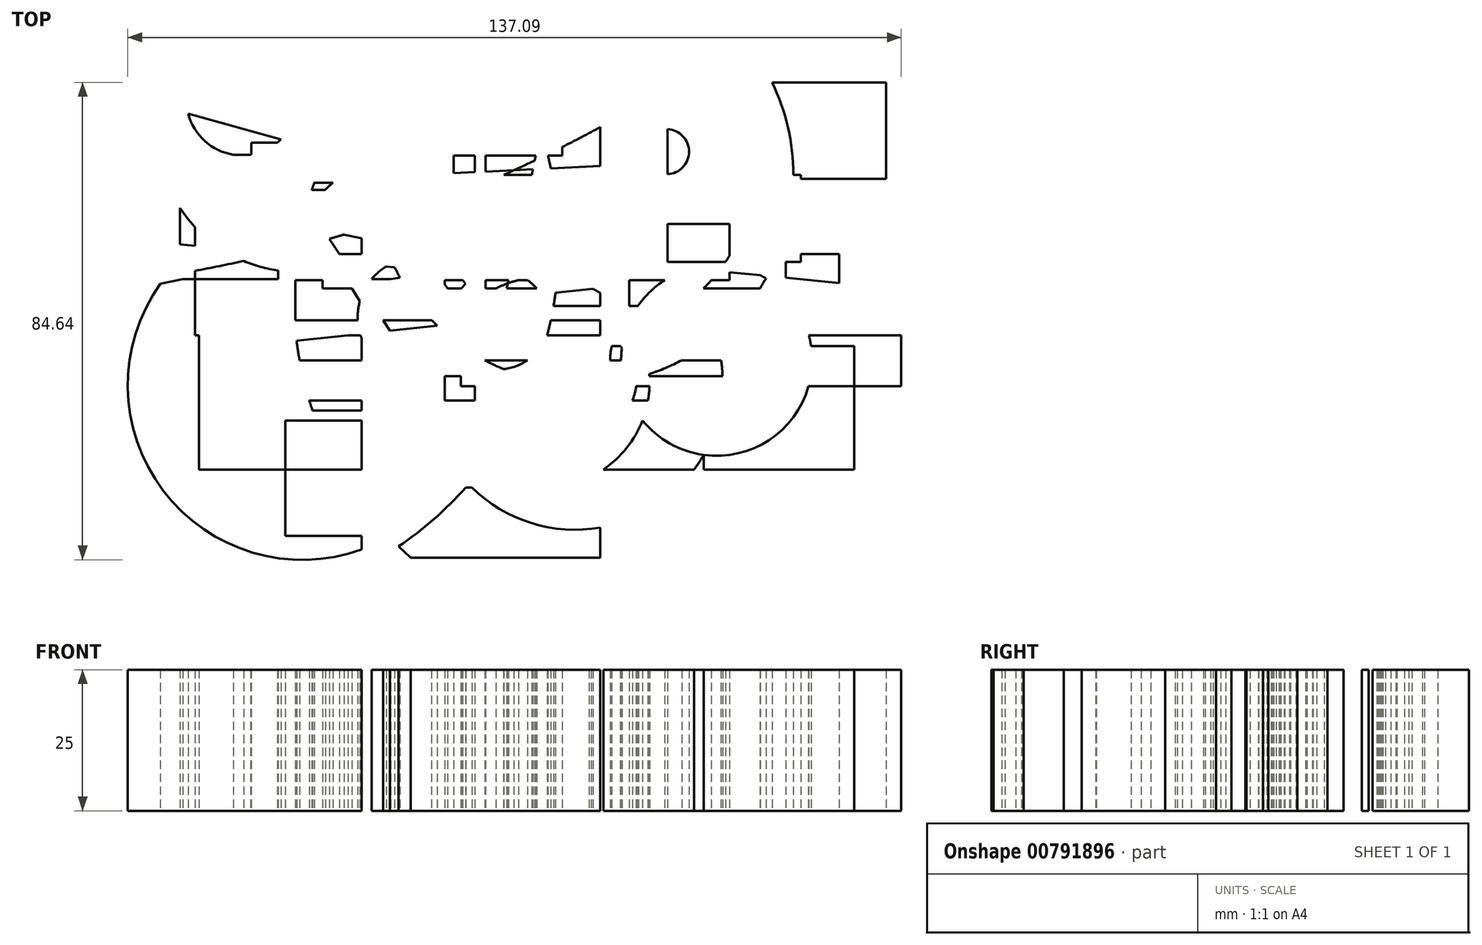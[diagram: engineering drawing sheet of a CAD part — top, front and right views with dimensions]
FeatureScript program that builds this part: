
annotation { "Feature Type Name" : "Feature", "Feature Type Description" : "" }
export const myFeature = defineFeature(function(context is Context, id is Id, definition is map)
    precondition{}
    {
        {
            var Q0;
            Q0=qCreatedBy(makeId("Top.planeOp"),FACE);
            var sketch = newSketch(context, id + "F0", { "sketchPlane" : qUnion([Q0])});
            skLineSegment(sketch, "E0.bottom", {"start": v(-53.43, 52.18) * mm, "end": v(-24.63, 52.18) * mm});
            skLineSegment(sketch, "E0.top", {"start": v(-53.43, 23.56) * mm, "end": v(-24.63, 23.56) * mm});
            skLineSegment(sketch, "E0.left", {"start": v(-53.43, 52.18) * mm, "end": v(-53.43, 23.56) * mm});
            skLineSegment(sketch, "E0.right", {"start": v(-24.63, 52.18) * mm, "end": v(-24.63, 23.56) * mm});
            skLineSegment(sketch, "E1.bottom", {"start": v(13.6, 38.85) * mm, "end": v(-31.38, 38.85) * mm});
            skLineSegment(sketch, "E1.top", {"start": v(13.6, 23.56) * mm, "end": v(-31.38, 23.56) * mm});
            skLineSegment(sketch, "E1.left", {"start": v(13.6, 38.85) * mm, "end": v(13.6, 23.56) * mm});
            skLineSegment(sketch, "E1.right", {"start": v(-31.38, 38.85) * mm, "end": v(-31.38, 23.56) * mm});
            skLineSegment(sketch, "E2.bottom", {"start": v(-41.52, 25.87) * mm, "end": v(-5.6, 25.87) * mm});
            skLineSegment(sketch, "E2.top", {"start": v(-41.52, 4.71) * mm, "end": v(-5.6, 4.71) * mm});
            skLineSegment(sketch, "E2.left", {"start": v(-41.52, 25.87) * mm, "end": v(-41.52, 4.71) * mm});
            skLineSegment(sketch, "E2.right", {"start": v(-5.6, 25.87) * mm, "end": v(-5.6, 4.71) * mm});
            skLineSegment(sketch, "E3.bottom", {"start": v(24.98, 4.71) * mm, "end": v(-33.7, 4.71) * mm});
            skLineSegment(sketch, "E3.top", {"start": v(24.98, -15.56) * mm, "end": v(-33.7, -15.56) * mm});
            skLineSegment(sketch, "E3.left", {"start": v(24.98, 4.71) * mm, "end": v(24.98, -15.56) * mm});
            skLineSegment(sketch, "E3.right", {"start": v(-33.7, 4.71) * mm, "end": v(-33.7, -15.56) * mm});
            skLineSegment(sketch, "E4.bottom", {"start": v(-35.47, -21.6) * mm, "end": v(38.67, -21.6) * mm});
            skLineSegment(sketch, "E4.top", {"start": v(-35.47, -43.83) * mm, "end": v(38.67, -43.83) * mm});
            skLineSegment(sketch, "E4.left", {"start": v(-35.47, -21.6) * mm, "end": v(-35.47, -43.83) * mm});
            skLineSegment(sketch, "E4.right", {"start": v(38.67, -21.6) * mm, "end": v(38.67, -43.83) * mm});
            skLineSegment(sketch, "E5.bottom", {"start": v(85.26, -17.34) * mm, "end": v(-4.36, -17.34) * mm});
            skLineSegment(sketch, "E5.top", {"start": v(85.26, -15.56) * mm, "end": v(-4.36, -15.56) * mm});
            skLineSegment(sketch, "E5.left", {"start": v(85.26, -17.34) * mm, "end": v(85.26, -15.56) * mm});
            skLineSegment(sketch, "E5.right", {"start": v(-4.36, -17.34) * mm, "end": v(-4.36, -15.56) * mm});
            skLineSegment(sketch, "E6.bottom", {"start": v(-50.76, -8.27) * mm, "end": v(95.03, -8.27) * mm});
            skLineSegment(sketch, "E6.top", {"start": v(-50.76, -32.1) * mm, "end": v(95.03, -32.1) * mm});
            skLineSegment(sketch, "E6.left", {"start": v(-50.76, -8.27) * mm, "end": v(-50.76, -32.1) * mm});
            skLineSegment(sketch, "E6.right", {"start": v(95.03, -8.27) * mm, "end": v(95.03, -32.1) * mm});
            skLineSegment(sketch, "E7.bottom", {"start": v(40.1, 55.38) * mm, "end": v(23.74, 55.38) * mm});
            skLineSegment(sketch, "E7.top", {"start": v(40.1, 13.42) * mm, "end": v(23.74, 13.42) * mm});
            skLineSegment(sketch, "E7.left", {"start": v(40.1, 55.38) * mm, "end": v(40.1, 13.42) * mm});
            skLineSegment(sketch, "E7.right", {"start": v(23.74, 55.38) * mm, "end": v(23.74, 13.42) * mm});
            skLineSegment(sketch, "E8.bottom", {"start": v(-13.78, 4.71) * mm, "end": v(55.92, 4.71) * mm});
            skLineSegment(sketch, "E8.top", {"start": v(-13.78, 20.18) * mm, "end": v(55.92, 20.18) * mm});
            skLineSegment(sketch, "E8.left", {"start": v(-13.78, 4.71) * mm, "end": v(-13.78, 20.18) * mm});
            skLineSegment(sketch, "E8.right", {"start": v(55.92, 4.71) * mm, "end": v(55.92, 20.18) * mm});
            skLineSegment(sketch, "E9.bottom", {"start": v(79.39, 19.47) * mm, "end": v(-17.51, 19.47) * mm});
            skLineSegment(sketch, "E9.top", {"start": v(79.39, 11.47) * mm, "end": v(-17.51, 11.47) * mm});
            skLineSegment(sketch, "E9.left", {"start": v(79.39, 19.47) * mm, "end": v(79.39, 11.47) * mm});
            skLineSegment(sketch, "E9.right", {"start": v(-17.51, 19.47) * mm, "end": v(-17.51, 11.47) * mm});
            skLineSegment(sketch, "E10.bottom", {"start": v(-21.96, 34.76) * mm, "end": v(20.36, 34.76) * mm});
            skLineSegment(sketch, "E10.top", {"start": v(-21.96, -47.74) * mm, "end": v(20.36, -47.74) * mm});
            skLineSegment(sketch, "E10.left", {"start": v(-21.96, 34.76) * mm, "end": v(-21.96, -2.78) * mm});
            skLineSegment(sketch, "E10.right", {"start": v(20.36, 34.76) * mm, "end": v(20.36, -47.74) * mm});
            skLineSegment(sketch, "E11.bottom", {"start": v(62.67, 6.13) * mm, "end": v(-28.9, 6.13) * mm});
            skLineSegment(sketch, "E11.top", {"start": v(62.67, 0) * mm, "end": v(-28.9, 0) * mm});
            skLineSegment(sketch, "E11.left", {"start": v(62.67, 6.13) * mm, "end": v(62.67, 0) * mm});
            skLineSegment(sketch, "E11.right", {"start": v(-28.9, 6.13) * mm, "end": v(-28.9, 0) * mm});
            skLineSegment(sketch, "E12.bottom", {"start": v(-40.98, -5.6) * mm, "end": v(73.7, -5.6) * mm});
            skLineSegment(sketch, "E12.top", {"start": v(-40.98, -19.82) * mm, "end": v(73.7, -19.82) * mm});
            skLineSegment(sketch, "E12.left", {"start": v(-40.98, -5.6) * mm, "end": v(-40.98, -19.82) * mm});
            skLineSegment(sketch, "E12.right", {"start": v(73.7, -5.6) * mm, "end": v(73.7, -19.82) * mm});
            skLineSegment(sketch, "E13.bottom", {"start": v(71.03, -3.11) * mm, "end": v(0, -3.11) * mm});
            skLineSegment(sketch, "E13.top", {"start": v(71.03, 36.54) * mm, "end": v(0, 36.54) * mm});
            skLineSegment(sketch, "E13.left", {"start": v(71.03, -3.11) * mm, "end": v(71.03, 36.54) * mm});
            skLineSegment(sketch, "E13.right", {"start": v(0, -3.11) * mm, "end": v(0, 36.54) * mm});
            skLineSegment(sketch, "E14.bottom", {"start": v(-1.87, 32.8) * mm, "end": v(-7.2, 32.8) * mm});
            skLineSegment(sketch, "E14.top", {"start": v(-1.87, -35.3) * mm, "end": v(-7.2, -35.3) * mm});
            skLineSegment(sketch, "E14.left", {"start": v(-1.87, 32.8) * mm, "end": v(-1.87, -35.3) * mm});
            skLineSegment(sketch, "E14.right", {"start": v(-7.2, 32.8) * mm, "end": v(-7.2, -35.3) * mm});
            skLineSegment(sketch, "E15.bottom", {"start": v(-42.58, -23.38) * mm, "end": v(50.94, -23.38) * mm});
            skLineSegment(sketch, "E15.top", {"start": v(-42.58, -12.71) * mm, "end": v(50.94, -12.71) * mm});
            skLineSegment(sketch, "E15.left", {"start": v(-42.58, -23.38) * mm, "end": v(-42.58, -12.71) * mm});
            skLineSegment(sketch, "E15.right", {"start": v(50.94, -23.38) * mm, "end": v(50.94, -12.71) * mm});
            skLineSegment(sketch, "E16.bottom", {"start": v(53.25, -8.27) * mm, "end": v(-51.47, -8.27) * mm});
            skLineSegment(sketch, "E16.top", {"start": v(53.25, 17.16) * mm, "end": v(-51.47, 17.16) * mm});
            skLineSegment(sketch, "E16.left", {"start": v(53.25, -8.27) * mm, "end": v(53.25, 17.16) * mm});
            skLineSegment(sketch, "E16.right", {"start": v(-51.47, -8.27) * mm, "end": v(-51.47, 17.16) * mm});
            skLineSegment(sketch, "E17.bottom", {"start": v(-36.72, 17.51) * mm, "end": v(43.3, 17.51) * mm});
            skLineSegment(sketch, "E17.top", {"start": v(-36.72, 1.51) * mm, "end": v(43.3, 1.51) * mm});
            skLineSegment(sketch, "E17.left", {"start": v(-36.72, 17.51) * mm, "end": v(-36.72, 1.51) * mm});
            skLineSegment(sketch, "E17.right", {"start": v(43.3, 17.51) * mm, "end": v(43.3, 1.51) * mm});
            skLineSegment(sketch, "E18.bottom", {"start": v(65.34, -10.22) * mm, "end": v(-15.56, -10.22) * mm});
            skLineSegment(sketch, "E18.top", {"start": v(65.34, -32.1) * mm, "end": v(-15.56, -32.1) * mm});
            skLineSegment(sketch, "E18.left", {"start": v(65.34, -10.22) * mm, "end": v(65.34, -32.1) * mm});
            skLineSegment(sketch, "E18.right", {"start": v(-15.56, -10.22) * mm, "end": v(-15.56, -32.1) * mm});
            skLineSegment(sketch, "E19.bottom", {"start": v(-54.14, 1.69) * mm, "end": v(25.51, 1.69) * mm});
            skLineSegment(sketch, "E19.top", {"start": v(-54.14, 67.48) * mm, "end": v(25.51, 67.48) * mm});
            skLineSegment(sketch, "E19.left", {"start": v(-54.14, 1.69) * mm, "end": v(-54.14, 67.48) * mm});
            skLineSegment(sketch, "E19.right", {"start": v(25.51, 1.69) * mm, "end": v(25.51, 67.48) * mm});
            skLineSegment(sketch, "E20.bottom", {"start": v(25.51, 45.25) * mm, "end": v(32.27, 45.25) * mm});
            skLineSegment(sketch, "E20.top", {"start": v(25.51, -3.11) * mm, "end": v(32.27, -3.11) * mm});
            skLineSegment(sketch, "E20.left", {"start": v(25.51, 45.25) * mm, "end": v(25.51, -3.11) * mm});
            skLineSegment(sketch, "E20.right", {"start": v(32.27, 45.25) * mm, "end": v(32.27, -3.11) * mm});
            skLineSegment(sketch, "E21.bottom", {"start": v(-12, 23.74) * mm, "end": v(-55.56, 23.74) * mm});
            skLineSegment(sketch, "E21.top", {"start": v(-12, 18.76) * mm, "end": v(-55.56, 18.76) * mm});
            skLineSegment(sketch, "E21.left", {"start": v(-12, 23.74) * mm, "end": v(-12, 18.76) * mm});
            skLineSegment(sketch, "E21.right", {"start": v(-55.56, 23.74) * mm, "end": v(-55.56, 18.76) * mm});
            skCircle(sketch, "E22", {"center": v(-33.16, 28) * mm, "radius": 25.06 * mm});
            skCircle(sketch, "E23", {"center": v(14.31, 24.1) * mm, "radius": 34.24 * mm});
            skCircle(sketch, "E24", {"center": v(-51.83, 7.91) * mm, "radius": 64.83 * mm});
            skCircle(sketch, "E25", {"center": v(27.3, -1.87) * mm, "radius": 61.2 * mm});
            skArc(sketch, "E26", {"start": v(-2.22, -8.27) * mm, "mid": v(-21.98, -1.4) * mm, "end": v(-2.56, -9.18) * mm});
            skCircle(sketch, "E27", {"center": v(2.4, -5.6) * mm, "radius": 8.71 * mm});
            skCircle(sketch, "E28", {"center": v(40.98, -12.71) * mm, "radius": 16.93 * mm});
            skCircle(sketch, "E29", {"center": v(10.4, -16.62) * mm, "radius": 18.7 * mm});
            skCircle(sketch, "E30", {"center": v(34.4, -12.9) * mm, "radius": 12.31 * mm});
            skCircle(sketch, "E31", {"center": v(18.58, -16.45) * mm, "radius": 8.18 * mm});
            skCircle(sketch, "E32", {"center": v(10.93, -16.62) * mm, "radius": 4.98 * mm});
            skCircle(sketch, "E33", {"center": v(15.91, -16.62) * mm, "radius": 26.15 * mm});
            skArc(sketch, "E34", {"start": v(-13.78, 7.51) * mm, "mid": v(-57.86, -34.81) * mm, "end": v(-2.81, -8.27) * mm});
            skCircle(sketch, "E35", {"center": v(32.1, 24.27) * mm, "radius": 4 * mm});
            skCircle(sketch, "E36", {"center": v(17.34, 20.18) * mm, "radius": 37.24 * mm});
            skCircle(sketch, "E37", {"center": v(-22.5, 12.53) * mm, "radius": 7.7 * mm});
            skArc(sketch, "E38", {"start": v(-48.45, 41.7) * mm, "mid": v(-47.9, 24.84) * mm, "end": v(-33.34, 33.34) * mm});
            skArc(sketch, "E39", {"start": v(-2.04, 17.87) * mm, "mid": v(21.17, 29.08) * mm, "end": v(43.05, 42.7) * mm});
            skLineSegment(sketch, "E40", {"start": v(-33.52, 45.6) * mm, "end": v(-9.16, 14.5) * mm});
            skLineSegment(sketch, "E41", {"start": v(35.47, 22.5) * mm, "end": v(-32.27, 19.11) * mm});
            skLineSegment(sketch, "E42", {"start": v(-53.96, 31.38) * mm, "end": v(-10.58, 19.3) * mm});
            skLineSegment(sketch, "E43", {"start": v(20.71, 30.31) * mm, "end": v(-39.92, 19.82) * mm});
            skLineSegment(sketch, "E44", {"start": v(-37.43, 23.56) * mm, "end": v(-14.5, -11.11) * mm});
            skLineSegment(sketch, "E45", {"start": v(16.62, 21.42) * mm, "end": v(-29.07, 8.98) * mm});
            skLineSegment(sketch, "E46", {"start": v(-45.25, 13.96) * mm, "end": v(-21.96, 8.9) * mm});
            skLineSegment(sketch, "E47", {"start": v(34.94, 1.51) * mm, "end": v(-15.38, -3.47) * mm});
            skLineSegment(sketch, "E48", {"start": v(-45.78, -10.58) * mm, "end": v(-4.53, -6.13) * mm});
            skLineSegment(sketch, "E49", {"start": v(25.16, 8.09) * mm, "end": v(-19.11, 1.33) * mm});
            skLineSegment(sketch, "E50", {"start": v(-52.54, 5.96) * mm, "end": v(5.25, 15.74) * mm});
            skLineSegment(sketch, "E51", {"start": v(-42.23, 4.18) * mm, "end": v(-104.28, -9.33) * mm});
            skLineSegment(sketch, "E52", {"start": v(-62.85, 8.8) * mm, "end": v(-28.9, 5.14) * mm});
            skLineSegment(sketch, "E53", {"start": v(62.85, 0.98) * mm, "end": v(-14.31, 8.45) * mm});
            skLineSegment(sketch, "E54", {"start": v(-38.5, 23.74) * mm, "end": v(4.53, -45.25) * mm});
            skLineSegment(sketch, "E55", {"start": v(10.4, 30.31) * mm, "end": v(2.76, -4.71) * mm});
            skLineSegment(sketch, "E56", {"start": v(-0.98, 21.07) * mm, "end": v(-8.09, 15.56) * mm});
            skLineSegment(sketch, "E57.trimOffspring", {"start": v(-26.75, 4.9) * mm, "end": v(4.71, 1.51) * mm});
            skArc(sketch, "E58.trimOffspring", {"start": v(-3.75, -5.6) * mm, "mid": v(-7.6, 1.28) * mm, "end": v(-13.07, 6.96) * mm});
            skArc(sketch, "E59.trimOffspring", {"start": v(-51.47, 3.14) * mm, "mid": v(-35.15, 6.75) * mm, "end": v(-19.11, 11.47) * mm});
            skLineSegment(sketch, "E60.trimOffspring", {"start": v(-21.96, -5.6) * mm, "end": v(-21.96, -47.74) * mm});
            skLineSegment(sketch, "E61.trimOffspring", {"start": v(-18.02, 8.04) * mm, "end": v(3.82, 3.29) * mm});
            skSolve(sketch);
        }
        {
            var Q0;
            {var subQ6=sQuery(id+"F0.wireOp",EDGE,"E2.left");var subQ7=sQuery(id+"F0.wireOp",EDGE,"E2.bottom");var subQ8=makeQuery(id+"F0.imprint","INTERSECT",VERTEX,{"derivedFrom":[subQ7,subQ6]});Q0=makeQuery(id+"F0.imprint","IMPRINT",FACE,{"disambiguationData":[TD([[makeQuery(id+"F0.imprint","IMPRINT",EDGE,{"disambiguationData":[TD([[subQ8,-1.0]])],"derivedFrom":subQ7}),1.0]])]});}
            var Q1;
            {var subQ0=sQuery(id+"F0.wireOp",EDGE,"E25");var subQ1=sQuery(id+"F0.wireOp",EDGE,"E17.bottom");var subQ2=makeQuery(id+"F0.imprint","INTERSECT",VERTEX,{"derivedFrom":[subQ1,subQ0]});Q1=makeQuery(id+"F0.imprint","IMPRINT",FACE,{"disambiguationData":[TD([[makeQuery(id+"F0.imprint","IMPRINT",EDGE,{"disambiguationData":[TD([[subQ2,-1.0]])],"derivedFrom":subQ1}),1.0]])]});}
            var Q2;
            {var subQ1=sQuery(id+"F0.wireOp",EDGE,"E19.bottom");var subQ5=sQuery(id+"F0.wireOp",EDGE,"E26");var subQ6=makeQuery(id+"F0.imprint","INTERSECT",VERTEX,{"disambiguationData":[OD(0.0)],"derivedFrom":[subQ1,subQ5]});Q2=makeQuery(id+"F0.imprint","IMPRINT",FACE,{"disambiguationData":[TD([[makeQuery(id+"F0.imprint","IMPRINT",EDGE,{"disambiguationData":[TD([[subQ6,-1.0]])],"derivedFrom":subQ1}),1.0]])]});}
            var Q3;
            {var subQ5=sQuery(id+"F0.wireOp",EDGE,"E27");var subQ6=sQuery(id+"F0.wireOp",EDGE,"E11.top");var subQ7=makeQuery(id+"F0.imprint","INTERSECT",VERTEX,{"disambiguationData":[OD(1.0)],"derivedFrom":[subQ6,subQ5]});Q3=makeQuery(id+"F0.imprint","IMPRINT",FACE,{"disambiguationData":[TD([[makeQuery(id+"F0.imprint","IMPRINT",EDGE,{"disambiguationData":[TD([[subQ7,-1.0]])],"derivedFrom":subQ6}),-1.0]])]});}
            var Q4;
            {var subQ0=sQuery(id+"F0.wireOp",EDGE,"E29");var subQ1=sQuery(id+"F0.wireOp",EDGE,"E11.top");var subQ2=makeQuery(id+"F0.imprint","INTERSECT",VERTEX,{"disambiguationData":[OD(1.0)],"derivedFrom":[subQ1,subQ0]});Q4=makeQuery(id+"F0.imprint","IMPRINT",FACE,{"disambiguationData":[TD([[makeQuery(id+"F0.imprint","IMPRINT",EDGE,{"disambiguationData":[TD([[subQ2,-1.0]])],"derivedFrom":subQ1}),-1.0]])]});}
            var Q5;
            {var subQ0=sQuery(id+"F0.wireOp",EDGE,"E27");var subQ1=sQuery(id+"F0.wireOp",EDGE,"E11.top");var subQ2=makeQuery(id+"F0.imprint","INTERSECT",VERTEX,{"disambiguationData":[OD(0.0)],"derivedFrom":[subQ1,subQ0]});Q5=makeQuery(id+"F0.imprint","IMPRINT",FACE,{"disambiguationData":[TD([[makeQuery(id+"F0.imprint","IMPRINT",EDGE,{"disambiguationData":[TD([[subQ2,-1.0]])],"derivedFrom":subQ1}),-1.0]])]});}
            var Q6;
            {var subQ0=sQuery(id+"F0.wireOp",EDGE,"E31");var subQ1=sQuery(id+"F0.wireOp",EDGE,"E18.bottom");var subQ2=makeQuery(id+"F0.imprint","INTERSECT",VERTEX,{"disambiguationData":[OD(1.0)],"derivedFrom":[subQ1,subQ0]});Q6=makeQuery(id+"F0.imprint","IMPRINT",FACE,{"disambiguationData":[TD([[makeQuery(id+"F0.imprint","IMPRINT",EDGE,{"disambiguationData":[TD([[subQ2,-1.0]])],"derivedFrom":subQ1}),1.0]])]});}
            var Q7;
            {var subQ0=sQuery(id+"F0.wireOp",EDGE,"E36");var subQ1=sQuery(id+"F0.wireOp",EDGE,"E15.top");var subQ2=makeQuery(id+"F0.imprint","INTERSECT",VERTEX,{"disambiguationData":[OD(0.0)],"derivedFrom":[subQ1,subQ0]});Q7=makeQuery(id+"F0.imprint","IMPRINT",FACE,{"disambiguationData":[TD([[makeQuery(id+"F0.imprint","IMPRINT",EDGE,{"disambiguationData":[TD([[subQ2,-1.0]])],"derivedFrom":subQ1}),-1.0]])]});}
            var Q8;
            {var subQ0=sQuery(id+"F0.wireOp",EDGE,"E44");var subQ1=sQuery(id+"F0.wireOp",EDGE,"E12.bottom");var subQ2=makeQuery(id+"F0.imprint","INTERSECT",VERTEX,{"derivedFrom":[subQ1,subQ0]});Q8=makeQuery(id+"F0.imprint","IMPRINT",FACE,{"disambiguationData":[TD([[makeQuery(id+"F0.imprint","IMPRINT",EDGE,{"disambiguationData":[TD([[subQ2,-1.0]])],"derivedFrom":subQ1}),-1.0]])]});}
            var Q9;
            {var subQ0=sQuery(id+"F0.wireOp",EDGE,"E25");var subQ1=sQuery(id+"F0.wireOp",EDGE,"E6.top");var subQ2=makeQuery(id+"F0.imprint","INTERSECT",VERTEX,{"disambiguationData":[OD(1.0)],"derivedFrom":[subQ1,subQ0]});Q9=makeQuery(id+"F0.imprint","IMPRINT",FACE,{"disambiguationData":[TD([[makeQuery(id+"F0.imprint","IMPRINT",EDGE,{"disambiguationData":[TD([[subQ2,-1.0]])],"derivedFrom":subQ1}),1.0]])]});}
            var Q10;
            {var subQ0=sQuery(id+"F0.wireOp",EDGE,"E15.bottom");var subQ1=sQuery(id+"F0.wireOp",EDGE,"E4.left");var subQ2=makeQuery(id+"F0.imprint","INTERSECT",VERTEX,{"derivedFrom":[subQ1,subQ0]});Q10=makeQuery(id+"F0.imprint","IMPRINT",FACE,{"disambiguationData":[TD([[makeQuery(id+"F0.imprint","IMPRINT",EDGE,{"disambiguationData":[TD([[subQ2,-1.0]])],"derivedFrom":subQ1}),1.0]])]});}
            var Q11;
            {var subQ0=sQuery(id+"F0.wireOp",EDGE,"E29");var subQ9=sQuery(id+"F0.wireOp",EDGE,"E10.right");var subQ10=makeQuery(id+"F0.imprint","INTERSECT",VERTEX,{"disambiguationData":[OD(1.0)],"derivedFrom":[subQ9,subQ0]});Q11=makeQuery(id+"F0.imprint","IMPRINT",FACE,{"disambiguationData":[TD([[makeQuery(id+"F0.imprint","IMPRINT",EDGE,{"disambiguationData":[TD([[subQ10,-1.0]])],"derivedFrom":subQ9}),-1.0]])]});}
            var Q12;
            {var subQ3=sQuery(id+"F0.wireOp",EDGE,"E54");var subQ6=sQuery(id+"F0.wireOp",EDGE,"E4.top");var subQ9=makeQuery(id+"F0.imprint","INTERSECT",VERTEX,{"derivedFrom":[subQ6,subQ3]});Q12=makeQuery(id+"F0.imprint","IMPRINT",FACE,{"disambiguationData":[TD([[makeQuery(id+"F0.imprint","IMPRINT",EDGE,{"disambiguationData":[TD([[subQ9,1.0]])],"derivedFrom":subQ6}),1.0]])]});}
            var Q13;
            {var subQ3=sQuery(id+"F0.wireOp",EDGE,"E4.top");var subQ7=makeQuery(id+"F0.imprint","INTERSECT",VERTEX,{"derivedFrom":[subQ3,sQuery(id+"F0.wireOp",EDGE,"E54")]});Q13=makeQuery(id+"F0.imprint","IMPRINT",FACE,{"disambiguationData":[TD([[makeQuery(id+"F0.imprint","IMPRINT",EDGE,{"disambiguationData":[TD([[subQ7,1.0]])],"derivedFrom":subQ3}),-1.0]])]});}
            var Q14;
            {var subQ0=sQuery(id+"F0.wireOp",EDGE,"E28");var subQ1=sQuery(id+"F0.wireOp",EDGE,"E4.right");var subQ2=makeQuery(id+"F0.imprint","INTERSECT",VERTEX,{"derivedFrom":[subQ1,subQ0]});Q14=makeQuery(id+"F0.imprint","IMPRINT",FACE,{"disambiguationData":[TD([[makeQuery(id+"F0.imprint","IMPRINT",EDGE,{"disambiguationData":[TD([[subQ2,-1.0]])],"derivedFrom":subQ1}),-1.0]])]});}
            var Q15;
            {var subQ0=sQuery(id+"F0.wireOp",EDGE,"E29");var subQ1=sQuery(id+"F0.wireOp",EDGE,"E5.bottom");var subQ2=makeQuery(id+"F0.imprint","INTERSECT",VERTEX,{"derivedFrom":[subQ1,subQ0]});Q15=makeQuery(id+"F0.imprint","IMPRINT",FACE,{"disambiguationData":[TD([[makeQuery(id+"F0.imprint","IMPRINT",EDGE,{"disambiguationData":[TD([[subQ2,-1.0]])],"derivedFrom":subQ1}),1.0]])]});}
            var Q16;
            {var subQ1=sQuery(id+"F0.wireOp",EDGE,"E16.bottom");var subQ7=sQuery(id+"F0.wireOp",EDGE,"E33");var subQ8=makeQuery(id+"F0.imprint","INTERSECT",VERTEX,{"disambiguationData":[OD(0.0)],"derivedFrom":[subQ1,subQ7]});Q16=makeQuery(id+"F0.imprint","IMPRINT",FACE,{"disambiguationData":[TD([[makeQuery(id+"F0.imprint","IMPRINT",EDGE,{"disambiguationData":[TD([[subQ8,-1.0]])],"derivedFrom":subQ1}),1.0]])]});}
            var Q17;
            {var subQ1=sQuery(id+"F0.wireOp",EDGE,"E11.top");var subQ9=sQuery(id+"F0.wireOp",EDGE,"E36");var subQ10=makeQuery(id+"F0.imprint","INTERSECT",VERTEX,{"disambiguationData":[OD(0.0)],"derivedFrom":[subQ1,subQ9]});Q17=makeQuery(id+"F0.imprint","IMPRINT",FACE,{"disambiguationData":[TD([[makeQuery(id+"F0.imprint","IMPRINT",EDGE,{"disambiguationData":[TD([[subQ10,-1.0]])],"derivedFrom":subQ1}),-1.0]])]});}
            var Q18;
            {var subQ5=sQuery(id+"F0.wireOp",EDGE,"E20.right");var subQ7=sQuery(id+"F0.wireOp",EDGE,"E8.bottom");var subQ8=makeQuery(id+"F0.imprint","INTERSECT",VERTEX,{"derivedFrom":[subQ7,subQ5]});Q18=makeQuery(id+"F0.imprint","IMPRINT",FACE,{"disambiguationData":[TD([[makeQuery(id+"F0.imprint","IMPRINT",EDGE,{"disambiguationData":[TD([[subQ8,-1.0]])],"derivedFrom":subQ7}),1.0]])]});}
            var Q19;
            {var subQ0=sQuery(id+"F0.wireOp",EDGE,"E33");var subQ1=sQuery(id+"F0.wireOp",EDGE,"E10.right");var subQ2=makeQuery(id+"F0.imprint","INTERSECT",VERTEX,{"disambiguationData":[OD(0.0)],"derivedFrom":[subQ1,subQ0]});Q19=makeQuery(id+"F0.imprint","IMPRINT",FACE,{"disambiguationData":[TD([[makeQuery(id+"F0.imprint","IMPRINT",EDGE,{"disambiguationData":[TD([[subQ2,-1.0]])],"derivedFrom":subQ1}),-1.0]])]});}
            var Q20;
            {var subQ1=sQuery(id+"F0.wireOp",EDGE,"E10.right");var subQ5=sQuery(id+"F0.wireOp",EDGE,"E12.bottom");var subQ6=makeQuery(id+"F0.imprint","INTERSECT",VERTEX,{"derivedFrom":[subQ1,subQ5]});Q20=makeQuery(id+"F0.imprint","IMPRINT",FACE,{"disambiguationData":[TD([[makeQuery(id+"F0.imprint","IMPRINT",EDGE,{"disambiguationData":[TD([[subQ6,-1.0]])],"derivedFrom":subQ1}),-1.0]])]});}
            var Q21;
            {var subQ0=sQuery(id+"F0.wireOp",EDGE,"E18.left");var subQ1=sQuery(id+"F0.wireOp",EDGE,"E5.bottom");var subQ2=makeQuery(id+"F0.imprint","INTERSECT",VERTEX,{"derivedFrom":[subQ1,subQ0]});Q21=makeQuery(id+"F0.imprint","IMPRINT",FACE,{"disambiguationData":[TD([[makeQuery(id+"F0.imprint","IMPRINT",EDGE,{"disambiguationData":[TD([[subQ2,-1.0]])],"derivedFrom":subQ1}),1.0]])]});}
            var Q22;
            {var subQ0=sQuery(id+"F0.wireOp",EDGE,"E12.right");var subQ1=sQuery(id+"F0.wireOp",EDGE,"E5.bottom");var subQ2=makeQuery(id+"F0.imprint","INTERSECT",VERTEX,{"derivedFrom":[subQ1,subQ0]});Q22=makeQuery(id+"F0.imprint","IMPRINT",FACE,{"disambiguationData":[TD([[makeQuery(id+"F0.imprint","IMPRINT",EDGE,{"disambiguationData":[TD([[subQ2,-1.0]])],"derivedFrom":subQ1}),-1.0]])]});}
            var Q23;
            {var subQ5=sQuery(id+"F0.wireOp",EDGE,"E12.right");var subQ6=sQuery(id+"F0.wireOp",EDGE,"E5.top");var subQ7=makeQuery(id+"F0.imprint","INTERSECT",VERTEX,{"derivedFrom":[subQ6,subQ5]});Q23=makeQuery(id+"F0.imprint","IMPRINT",FACE,{"disambiguationData":[TD([[makeQuery(id+"F0.imprint","IMPRINT",EDGE,{"disambiguationData":[TD([[subQ7,-1.0]])],"derivedFrom":subQ6}),-1.0]])]});}
            var Q24;
            {var subQ7=sQuery(id+"F0.wireOp",EDGE,"E4.right");var subQ9=sQuery(id+"F0.wireOp",EDGE,"E33");var subQ10=makeQuery(id+"F0.imprint","INTERSECT",VERTEX,{"derivedFrom":[subQ7,subQ9]});Q24=makeQuery(id+"F0.imprint","IMPRINT",FACE,{"disambiguationData":[TD([[makeQuery(id+"F0.imprint","IMPRINT",EDGE,{"disambiguationData":[TD([[subQ10,-1.0]])],"derivedFrom":subQ7}),1.0]])]});}
            var Q25;
            {var subQ1=sQuery(id+"F0.wireOp",EDGE,"E5.top");var subQ7=sQuery(id+"F0.wireOp",EDGE,"E33");var subQ9=makeQuery(id+"F0.imprint","INTERSECT",VERTEX,{"derivedFrom":[subQ1,subQ7]});Q25=makeQuery(id+"F0.imprint","IMPRINT",FACE,{"disambiguationData":[TD([[makeQuery(id+"F0.imprint","IMPRINT",EDGE,{"disambiguationData":[TD([[subQ9,-1.0]])],"derivedFrom":subQ1}),-1.0]])]});}
            var Q26;
            {var subQ5=sQuery(id+"F0.wireOp",EDGE,"E5.right");Q26=makeQuery(id+"F0.imprint","IMPRINT",FACE,{"disambiguationData":[TD([[makeQuery(id+"F0.imprint","IMPRINT",EDGE,{"derivedFrom":subQ5}),1.0]])]});}
            var Q27;
            {var subQ0=sQuery(id+"F0.wireOp",EDGE,"E25");var subQ1=sQuery(id+"F0.wireOp",EDGE,"E4.bottom");var subQ2=makeQuery(id+"F0.imprint","INTERSECT",VERTEX,{"derivedFrom":[subQ1,subQ0]});Q27=makeQuery(id+"F0.imprint","IMPRINT",FACE,{"disambiguationData":[TD([[makeQuery(id+"F0.imprint","IMPRINT",EDGE,{"disambiguationData":[TD([[subQ2,-1.0]])],"derivedFrom":subQ1}),1.0]])]});}
            var Q28;
            {var subQ5=sQuery(id+"F0.wireOp",EDGE,"E46");var subQ6=sQuery(id+"F0.wireOp",EDGE,"E10.left");var subQ7=makeQuery(id+"F0.imprint","INTERSECT",VERTEX,{"derivedFrom":[subQ6,subQ5]});Q28=makeQuery(id+"F0.imprint","IMPRINT",FACE,{"disambiguationData":[TD([[makeQuery(id+"F0.imprint","IMPRINT",EDGE,{"disambiguationData":[TD([[subQ7,-1.0]])],"derivedFrom":subQ6}),-1.0]])]});}
            var Q29;
            {var subQ5=sQuery(id+"F0.wireOp",EDGE,"E55");var subQ6=sQuery(id+"F0.wireOp",EDGE,"E1.top");var subQ7=makeQuery(id+"F0.imprint","INTERSECT",VERTEX,{"derivedFrom":[subQ6,subQ5]});Q29=makeQuery(id+"F0.imprint","IMPRINT",FACE,{"disambiguationData":[TD([[makeQuery(id+"F0.imprint","IMPRINT",EDGE,{"disambiguationData":[TD([[subQ7,-1.0]])],"derivedFrom":subQ6}),1.0]])]});}
            var Q30;
            {var subQ6=sQuery(id+"F0.wireOp",EDGE,"E1.top");var subQ9=sQuery(id+"F0.wireOp",EDGE,"E1.left");var subQ10=makeQuery(id+"F0.imprint","INTERSECT",VERTEX,{"derivedFrom":[subQ6,subQ9]});Q30=makeQuery(id+"F0.imprint","IMPRINT",FACE,{"disambiguationData":[TD([[makeQuery(id+"F0.imprint","IMPRINT",EDGE,{"disambiguationData":[TD([[subQ10,-1.0]])],"derivedFrom":subQ6}),1.0]])]});}
            var Q31;
            {var subQ0=sQuery(id+"F0.wireOp",EDGE,"E39");var subQ1=sQuery(id+"F0.wireOp",EDGE,"E20.left");var subQ2=makeQuery(id+"F0.imprint","INTERSECT",VERTEX,{"derivedFrom":[subQ1,subQ0]});Q31=makeQuery(id+"F0.imprint","IMPRINT",FACE,{"disambiguationData":[TD([[makeQuery(id+"F0.imprint","IMPRINT",EDGE,{"disambiguationData":[TD([[subQ2,-1.0]])],"derivedFrom":subQ1}),1.0]])]});}
            var Q32;
            {var subQ0=sQuery(id+"F0.wireOp",EDGE,"E17.right");var subQ1=sQuery(id+"F0.wireOp",EDGE,"E9.top");var subQ2=makeQuery(id+"F0.imprint","INTERSECT",VERTEX,{"derivedFrom":[subQ1,subQ0]});Q32=makeQuery(id+"F0.imprint","IMPRINT",FACE,{"disambiguationData":[TD([[makeQuery(id+"F0.imprint","IMPRINT",EDGE,{"disambiguationData":[TD([[subQ2,-1.0]])],"derivedFrom":subQ1}),1.0]])]});}
            var Q33;
            {var subQ0=sQuery(id+"F0.wireOp",EDGE,"E28");var subQ1=sQuery(id+"F0.wireOp",EDGE,"E11.top");var subQ2=makeQuery(id+"F0.imprint","INTERSECT",VERTEX,{"disambiguationData":[OD(0.0)],"derivedFrom":[subQ1,subQ0]});Q33=makeQuery(id+"F0.imprint","IMPRINT",FACE,{"disambiguationData":[TD([[makeQuery(id+"F0.imprint","IMPRINT",EDGE,{"disambiguationData":[TD([[subQ2,-1.0]])],"derivedFrom":subQ1}),1.0]])]});}
            var Q34;
            {var subQ5=sQuery(id+"F0.wireOp",EDGE,"E8.right");var subQ7=sQuery(id+"F0.wireOp",EDGE,"E8.bottom");var subQ8=makeQuery(id+"F0.imprint","INTERSECT",VERTEX,{"derivedFrom":[subQ7,subQ5]});Q34=makeQuery(id+"F0.imprint","IMPRINT",FACE,{"disambiguationData":[TD([[makeQuery(id+"F0.imprint","IMPRINT",EDGE,{"disambiguationData":[TD([[subQ8,1.0]])],"derivedFrom":subQ7}),-1.0]])]});}
            var Q35;
            {var subQ1=sQuery(id+"F0.wireOp",EDGE,"E8.right");var subQ5=sQuery(id+"F0.wireOp",EDGE,"E8.top");var subQ6=makeQuery(id+"F0.imprint","INTERSECT",VERTEX,{"derivedFrom":[subQ5,subQ1]});Q35=makeQuery(id+"F0.imprint","IMPRINT",FACE,{"disambiguationData":[TD([[makeQuery(id+"F0.imprint","IMPRINT",EDGE,{"disambiguationData":[TD([[subQ6,1.0]])],"derivedFrom":subQ5}),1.0]])]});}
            var Q36;
            {var subQ0=sQuery(id+"F0.wireOp",EDGE,"E20.right");var subQ1=makeQuery(id+"F0.imprint","INTERSECT",VERTEX,{"derivedFrom":[subQ0,sQuery(id+"F0.wireOp",EDGE,"E41")]});Q36=makeQuery(id+"F0.imprint","IMPRINT",FACE,{"disambiguationData":[TD([[makeQuery(id+"F0.imprint","IMPRINT",EDGE,{"disambiguationData":[TD([[subQ1,1.0]])],"derivedFrom":subQ0}),1.0]])]});}
            var Q37;
            {var subQ0=sQuery(id+"F0.wireOp",EDGE,"E39");var subQ1=sQuery(id+"F0.wireOp",EDGE,"E8.top");var subQ2=makeQuery(id+"F0.imprint","INTERSECT",VERTEX,{"derivedFrom":[subQ1,subQ0]});Q37=makeQuery(id+"F0.imprint","IMPRINT",FACE,{"disambiguationData":[TD([[makeQuery(id+"F0.imprint","IMPRINT",EDGE,{"disambiguationData":[TD([[subQ2,-1.0]])],"derivedFrom":subQ1}),1.0]])]});}
            var Q38;
            {var subQ0=sQuery(id+"F0.wireOp",EDGE,"E14.left");var subQ1=sQuery(id+"F0.wireOp",EDGE,"E1.top");var subQ2=makeQuery(id+"F0.imprint","INTERSECT",VERTEX,{"derivedFrom":[subQ1,subQ0]});Q38=makeQuery(id+"F0.imprint","IMPRINT",FACE,{"disambiguationData":[TD([[makeQuery(id+"F0.imprint","IMPRINT",EDGE,{"disambiguationData":[TD([[subQ2,-1.0]])],"derivedFrom":subQ1}),1.0]])]});}
            var Q39;
            {var subQ1=sQuery(id+"F0.wireOp",EDGE,"E3.right");var subQ10=sQuery(id+"F0.wireOp",EDGE,"E17.top");var subQ12=makeQuery(id+"F0.imprint","INTERSECT",VERTEX,{"derivedFrom":[subQ1,subQ10]});Q39=makeQuery(id+"F0.imprint","IMPRINT",FACE,{"disambiguationData":[TD([[makeQuery(id+"F0.imprint","IMPRINT",EDGE,{"disambiguationData":[TD([[subQ12,-1.0]])],"derivedFrom":subQ1}),1.0]])]});}
            var Q40;
            {var subQ0=sQuery(id+"F0.wireOp",EDGE,"E25");var subQ1=sQuery(id+"F0.wireOp",EDGE,"E15.top");var subQ2=makeQuery(id+"F0.imprint","INTERSECT",VERTEX,{"derivedFrom":[subQ1,subQ0]});Q40=makeQuery(id+"F0.imprint","IMPRINT",FACE,{"disambiguationData":[TD([[makeQuery(id+"F0.imprint","IMPRINT",EDGE,{"disambiguationData":[TD([[subQ2,-1.0]])],"derivedFrom":subQ1}),1.0]])]});}
            var Q41;
            {var subQ1=sQuery(id+"F0.wireOp",EDGE,"E16.right");var subQ5=makeQuery(id+"F0.imprint","INTERSECT",VERTEX,{"derivedFrom":[subQ1,sQuery(id+"F0.wireOp",EDGE,"E51")]});Q41=makeQuery(id+"F0.imprint","IMPRINT",FACE,{"disambiguationData":[TD([[makeQuery(id+"F0.imprint","IMPRINT",EDGE,{"disambiguationData":[TD([[subQ5,1.0]])],"derivedFrom":subQ1}),-1.0]])]});}
            var Q42;
            {var subQ0=sQuery(id+"F0.wireOp",EDGE,"E52");var subQ1=sQuery(id+"F0.wireOp",EDGE,"E16.right");var subQ2=makeQuery(id+"F0.imprint","INTERSECT",VERTEX,{"derivedFrom":[subQ1,subQ0]});Q42=makeQuery(id+"F0.imprint","IMPRINT",FACE,{"disambiguationData":[TD([[makeQuery(id+"F0.imprint","IMPRINT",EDGE,{"disambiguationData":[TD([[subQ2,-1.0]])],"derivedFrom":subQ1}),1.0]])]});}
            extrude(context, id + "F1", {"entities" : qUnion([Q0, Q1, Q2, Q3, Q4, Q5, Q6, Q7, Q8, Q9, Q10, Q11, Q12, Q13, Q14, Q15, Q16, Q17, Q18, Q19, Q20, Q21, Q22, Q23, Q24, Q25, Q26, Q27, Q28, Q29, Q30, Q31, Q32, Q33, Q34, Q35, Q36, Q37, Q38, Q39, Q40, Q41, Q42]), "depth" : 25 * mm, "offsetDistance" : 25 * mm});
        }
    });
